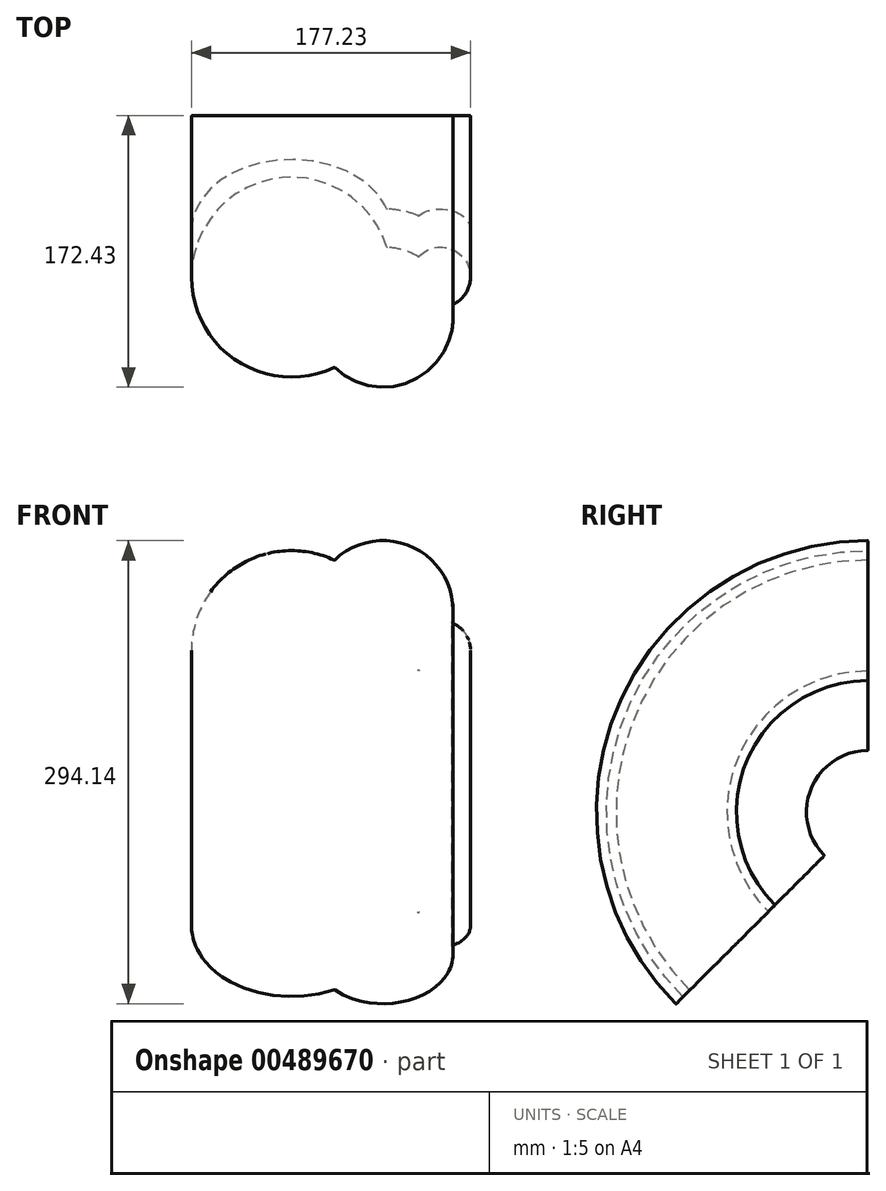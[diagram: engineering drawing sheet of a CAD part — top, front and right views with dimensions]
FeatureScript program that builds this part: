
annotation { "Feature Type Name" : "Feature", "Feature Type Description" : "" }
export const myFeature = defineFeature(function(context is Context, id is Id, definition is map)
    precondition{}
    {
        {
            var Q0;
            Q0=qCreatedBy(makeId("Front.planeOp"),FACE);
            var sketch = newSketch(context, id + "F0", { "sketchPlane" : qUnion([Q0])});
            skArc(sketch, "E0", {"start": v(26.97, 57.49) * mm, "mid": v(-58.2, -25.4) * mm, "end": v(60.5, -19.32) * mm});
            skArc(sketch, "E1", {"start": v(60.94, -18.97) * mm, "mid": v(70.98, -17.17) * mm, "end": v(80.35, -13.14) * mm});
            skArc(sketch, "E2", {"start": v(80.97, -13.23) * mm, "mid": v(110.31, -10.89) * mm, "end": v(102.32, 17.45) * mm});
            skLineSegment(sketch, "E3", {"start": v(0, 0) * mm, "end": v(94.68, 0) * mm, "construction": true});
            skLineSegment(sketch, "E4", {"start": v(0, 0) * mm, "end": v(0, -102.58) * mm, "construction": true});
            skLineSegment(sketch, "E5", {"start": v(0, -102.58) * mm, "end": v(97.7, -102.58) * mm, "construction": true});
            skArc(sketch, "E6.trimOffspring", {"start": v(102.03, 18) * mm, "mid": v(79.06, 64.65) * mm, "end": v(27.54, 57.58) * mm});
            skPoint(sketch, "E7.visualSharp", {"position": v(27.28, 57.34) * mm});
            skArc(sketch, "E7.filletArc", {"start": v(26.97, 57.49) * mm, "mid": v(27.27, 57.45) * mm, "end": v(27.54, 57.58) * mm});
            skPoint(sketch, "E8.visualSharp", {"position": v(60.6, -18.99) * mm});
            skArc(sketch, "E8.filletArc", {"start": v(60.94, -18.97) * mm, "mid": v(60.66, -19.07) * mm, "end": v(60.5, -19.32) * mm});
            skPoint(sketch, "E9.visualSharp", {"position": v(80.7, -12.94) * mm});
            skArc(sketch, "E9.filletArc", {"start": v(80.97, -13.23) * mm, "mid": v(80.67, -13.08) * mm, "end": v(80.35, -13.14) * mm});
            skPoint(sketch, "E10.visualSharp", {"position": v(101.96, 17.6) * mm});
            skArc(sketch, "E10.filletArc", {"start": v(102.03, 18) * mm, "mid": v(102.08, 17.67) * mm, "end": v(102.32, 17.45) * mm});
            skSolve(sketch);
        }
        {
            var Q0;
            Q0=makeQuery(id+"F0.imprint","IMPRINT",FACE,{"disambiguationData":[TD([[makeQuery(id+"F0.imprint","IMPRINT",EDGE,{"derivedFrom":sQuery(id+"F0.wireOp",EDGE,"E0")}),1.0]])]});
            var Q1;
            Q1=sQuery(id+"F0.wireOp",EDGE,"E5");
            revolve(context, id + "F1", {"entities" : qUnion([Q0]), "axis" : qUnion([Q1]), "revolveType" : RevolveType.ONE_DIRECTION, "angle" : 135 * degree});
        }
        {
            var Q0;
            Q0=makeQuery(id+"F1.opRevolve","CAP_FACE",FACE,{"disambiguationData":[OSD([sQuery(id+"F0.wireOp",EDGE,"E0"),sQuery(id+"F0.wireOp",EDGE,"E1"),sQuery(id+"F0.wireOp",EDGE,"E2"),sQuery(id+"F0.wireOp",EDGE,"E6.trimOffspring"),sQuery(id+"F0.wireOp",EDGE,"E7.filletArc"),sQuery(id+"F0.wireOp",EDGE,"E8.filletArc"),sQuery(id+"F0.wireOp",EDGE,"E9.filletArc"),sQuery(id+"F0.wireOp",EDGE,"E10.filletArc")])],"isStart":true});
            var Q1;
            Q1=makeQuery(id+"F1.opRevolve","CAP_FACE",FACE,{"disambiguationData":[OSD([sQuery(id+"F0.wireOp",EDGE,"E0"),sQuery(id+"F0.wireOp",EDGE,"E1"),sQuery(id+"F0.wireOp",EDGE,"E2"),sQuery(id+"F0.wireOp",EDGE,"E6.trimOffspring"),sQuery(id+"F0.wireOp",EDGE,"E7.filletArc"),sQuery(id+"F0.wireOp",EDGE,"E8.filletArc"),sQuery(id+"F0.wireOp",EDGE,"E9.filletArc"),sQuery(id+"F0.wireOp",EDGE,"E10.filletArc")])],"isStart":false});
            fillet(context, id + "F2", {"entities" : qUnion([Q0, Q1]), "radius" : 0.5 * mm, "tangentPropagation" : true, "allowEdgeOverflow" : false});
        }
    });
